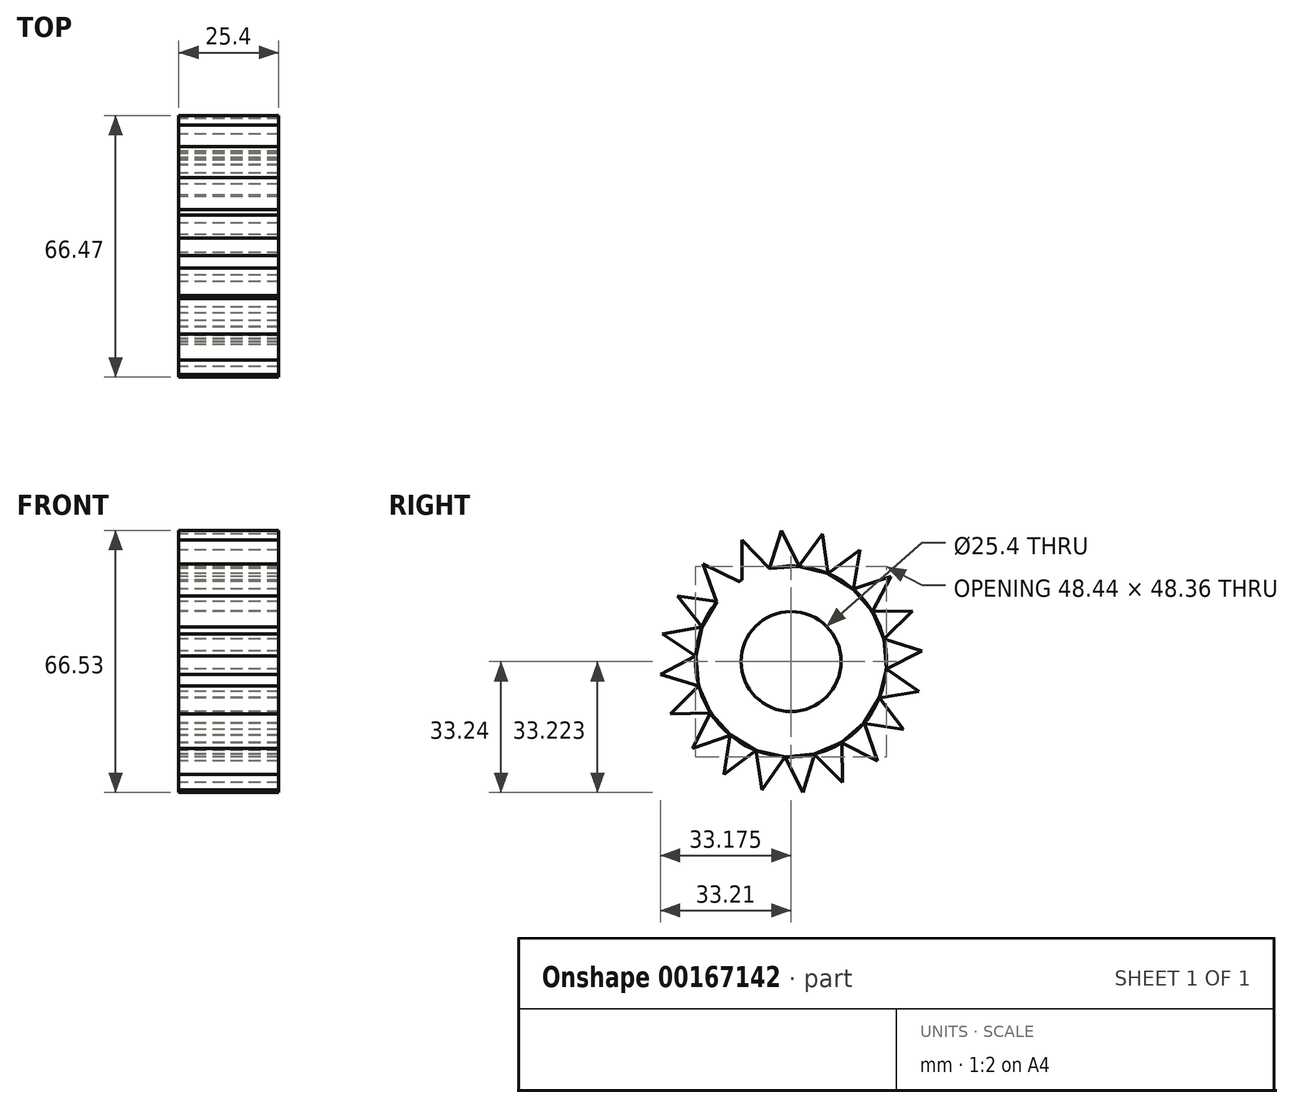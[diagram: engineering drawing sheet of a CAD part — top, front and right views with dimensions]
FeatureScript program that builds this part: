
annotation { "Feature Type Name" : "Feature", "Feature Type Description" : "" }
export const myFeature = defineFeature(function(context is Context, id is Id, definition is map)
    precondition{}
    {
        {
            var Q0;
            Q0=qCreatedBy(makeId("Right.planeOp"),FACE);
            var sketch = newSketch(context, id + "F0", { "sketchPlane" : qUnion([Q0])});
            skCircle(sketch, "E0", {"center": v(0, 0) * mm, "radius": 24.26 * mm});
            skLineSegment(sketch, "E1", {"start": v(-12.52, 20.78) * mm, "end": v(-12.52, 30.94) * mm});
            skLineSegment(sketch, "E2", {"start": v(-12.52, 30.94) * mm, "end": v(-5.45, 23.64) * mm});
            skLineSegment(sketch, "E3", {"start": v(-5.45, 23.64) * mm, "end": v(-12.52, 20.78) * mm});
            skLineSegment(sketch, "E4.1.0", {"start": v(2.07, 24.17) * mm, "end": v(-5.53, 23.62) * mm});
            skLineSegment(sketch, "E4.1.1", {"start": v(-2.4, 33.29) * mm, "end": v(2.07, 24.17) * mm});
            skLineSegment(sketch, "E4.1.2", {"start": v(-5.53, 23.62) * mm, "end": v(-2.4, 33.29) * mm});
            skLineSegment(sketch, "E4.2.0", {"start": v(9.4, 22.36) * mm, "end": v(2, 24.17) * mm});
            skLineSegment(sketch, "E4.2.1", {"start": v(7.94, 32.42) * mm, "end": v(9.4, 22.36) * mm});
            skLineSegment(sketch, "E4.2.2", {"start": v(2, 24.17) * mm, "end": v(7.94, 32.42) * mm});
            skLineSegment(sketch, "E4.3.0", {"start": v(15.82, 18.4) * mm, "end": v(9.33, 22.4) * mm});
            skLineSegment(sketch, "E4.3.1", {"start": v(17.52, 28.4) * mm, "end": v(15.82, 18.4) * mm});
            skLineSegment(sketch, "E4.3.2", {"start": v(9.33, 22.4) * mm, "end": v(17.52, 28.4) * mm});
            skLineSegment(sketch, "E4.4.0", {"start": v(20.7, 12.64) * mm, "end": v(15.76, 18.44) * mm});
            skLineSegment(sketch, "E4.4.1", {"start": v(25.4, 21.65) * mm, "end": v(20.7, 12.64) * mm});
            skLineSegment(sketch, "E4.4.2", {"start": v(15.76, 18.44) * mm, "end": v(25.4, 21.65) * mm});
            skLineSegment(sketch, "E4.5.0", {"start": v(23.59, 5.67) * mm, "end": v(20.66, 12.7) * mm});
            skLineSegment(sketch, "E4.5.1", {"start": v(30.82, 12.8) * mm, "end": v(23.59, 5.67) * mm});
            skLineSegment(sketch, "E4.5.2", {"start": v(20.66, 12.7) * mm, "end": v(30.82, 12.8) * mm});
            skLineSegment(sketch, "E4.6.0", {"start": v(24.19, -1.85) * mm, "end": v(23.57, 5.74) * mm});
            skLineSegment(sketch, "E4.6.1", {"start": v(33.26, 2.7) * mm, "end": v(24.19, -1.85) * mm});
            skLineSegment(sketch, "E4.6.2", {"start": v(23.57, 5.74) * mm, "end": v(33.26, 2.7) * mm});
            skLineSegment(sketch, "E4.7.0", {"start": v(22.45, -9.2) * mm, "end": v(24.2, -1.78) * mm});
            skLineSegment(sketch, "E4.7.1", {"start": v(32.49, -7.64) * mm, "end": v(22.45, -9.2) * mm});
            skLineSegment(sketch, "E4.7.2", {"start": v(24.2, -1.78) * mm, "end": v(32.49, -7.64) * mm});
            skLineSegment(sketch, "E4.8.0", {"start": v(18.54, -15.65) * mm, "end": v(22.48, -9.12) * mm});
            skLineSegment(sketch, "E4.8.1", {"start": v(28.57, -17.26) * mm, "end": v(18.54, -15.65) * mm});
            skLineSegment(sketch, "E4.8.2", {"start": v(22.48, -9.12) * mm, "end": v(28.57, -17.26) * mm});
            skLineSegment(sketch, "E4.9.0", {"start": v(12.83, -20.59) * mm, "end": v(18.58, -15.59) * mm});
            skLineSegment(sketch, "E4.9.1", {"start": v(21.88, -25.2) * mm, "end": v(12.83, -20.59) * mm});
            skLineSegment(sketch, "E4.9.2", {"start": v(18.58, -15.59) * mm, "end": v(21.88, -25.2) * mm});
            skLineSegment(sketch, "E4.10.0", {"start": v(5.88, -23.53) * mm, "end": v(12.9, -20.55) * mm});
            skLineSegment(sketch, "E4.10.1", {"start": v(13.08, -30.7) * mm, "end": v(5.88, -23.53) * mm});
            skLineSegment(sketch, "E4.10.2", {"start": v(12.9, -20.55) * mm, "end": v(13.08, -30.7) * mm});
            skLineSegment(sketch, "E4.11.0", {"start": v(-1.63, -24.2) * mm, "end": v(5.96, -23.51) * mm});
            skLineSegment(sketch, "E4.11.1", {"start": v(3.01, -33.24) * mm, "end": v(-1.63, -24.2) * mm});
            skLineSegment(sketch, "E4.11.2", {"start": v(5.96, -23.51) * mm, "end": v(3.01, -33.24) * mm});
            skLineSegment(sketch, "E4.12.0", {"start": v(-8.99, -22.53) * mm, "end": v(-1.56, -24.2) * mm});
            skLineSegment(sketch, "E4.12.1", {"start": v(-7.34, -32.56) * mm, "end": v(-8.99, -22.53) * mm});
            skLineSegment(sketch, "E4.12.2", {"start": v(-1.56, -24.2) * mm, "end": v(-7.34, -32.56) * mm});
            skLineSegment(sketch, "E4.13.0", {"start": v(-15.48, -18.68) * mm, "end": v(-8.92, -22.56) * mm});
            skLineSegment(sketch, "E4.13.1", {"start": v(-17, -28.72) * mm, "end": v(-15.48, -18.68) * mm});
            skLineSegment(sketch, "E4.13.2", {"start": v(-8.92, -22.56) * mm, "end": v(-17, -28.72) * mm});
            skLineSegment(sketch, "E4.14.0", {"start": v(-20.47, -13.02) * mm, "end": v(-15.42, -18.73) * mm});
            skLineSegment(sketch, "E4.14.1", {"start": v(-25, -22.11) * mm, "end": v(-20.47, -13.02) * mm});
            skLineSegment(sketch, "E4.14.2", {"start": v(-15.42, -18.73) * mm, "end": v(-25, -22.11) * mm});
            skLineSegment(sketch, "E4.15.0", {"start": v(-23.48, -6.1) * mm, "end": v(-20.43, -13.08) * mm});
            skLineSegment(sketch, "E4.15.1", {"start": v(-30.58, -13.36) * mm, "end": v(-23.48, -6.1) * mm});
            skLineSegment(sketch, "E4.15.2", {"start": v(-20.43, -13.08) * mm, "end": v(-30.58, -13.36) * mm});
            skLineSegment(sketch, "E4.16.0", {"start": v(-24.22, 1.4) * mm, "end": v(-23.46, -6.17) * mm});
            skLineSegment(sketch, "E4.16.1", {"start": v(-33.2, -3.32) * mm, "end": v(-24.22, 1.4) * mm});
            skLineSegment(sketch, "E4.16.2", {"start": v(-23.46, -6.17) * mm, "end": v(-33.2, -3.32) * mm});
            skLineSegment(sketch, "E4.17.0", {"start": v(-22.61, 8.78) * mm, "end": v(-24.22, 1.33) * mm});
            skLineSegment(sketch, "E4.17.1", {"start": v(-32.62, 7.05) * mm, "end": v(-22.61, 8.78) * mm});
            skLineSegment(sketch, "E4.17.2", {"start": v(-24.22, 1.33) * mm, "end": v(-32.62, 7.05) * mm});
            skLineSegment(sketch, "E4.18.0", {"start": v(-18.82, 15.3) * mm, "end": v(-22.64, 8.71) * mm});
            skLineSegment(sketch, "E4.18.1", {"start": v(-28.88, 16.73) * mm, "end": v(-18.82, 15.3) * mm});
            skLineSegment(sketch, "E4.18.2", {"start": v(-22.64, 8.71) * mm, "end": v(-28.88, 16.73) * mm});
            skLineSegment(sketch, "E4.19.0", {"start": v(-13.2, 20.35) * mm, "end": v(-18.87, 15.25) * mm});
            skLineSegment(sketch, "E4.19.1", {"start": v(-22.34, 24.8) * mm, "end": v(-13.2, 20.35) * mm});
            skLineSegment(sketch, "E4.19.2", {"start": v(-18.87, 15.25) * mm, "end": v(-22.34, 24.8) * mm});
            skLineSegment(sketch, "E4.anchor1", {"start": v(0, 0) * mm, "end": v(-12.52, 20.78) * mm, "construction": true});
            skLineSegment(sketch, "E4.anchor2", {"start": v(0, 0) * mm, "end": v(-18.87, 15.25) * mm, "construction": true});
            skCircle(sketch, "E5", {"center": v(0, 0) * mm, "radius": 12.7 * mm});
            skSolve(sketch);
        }
        {
            var Q0;
            Q0 = qSketchRegion(id + "F0", true);
            extrude(context, id + "F1", {"entities" : qUnion([Q0]), "endBound" : BoundingType.SYMMETRIC, "depth" : 25.4 * mm});
        }
    });
